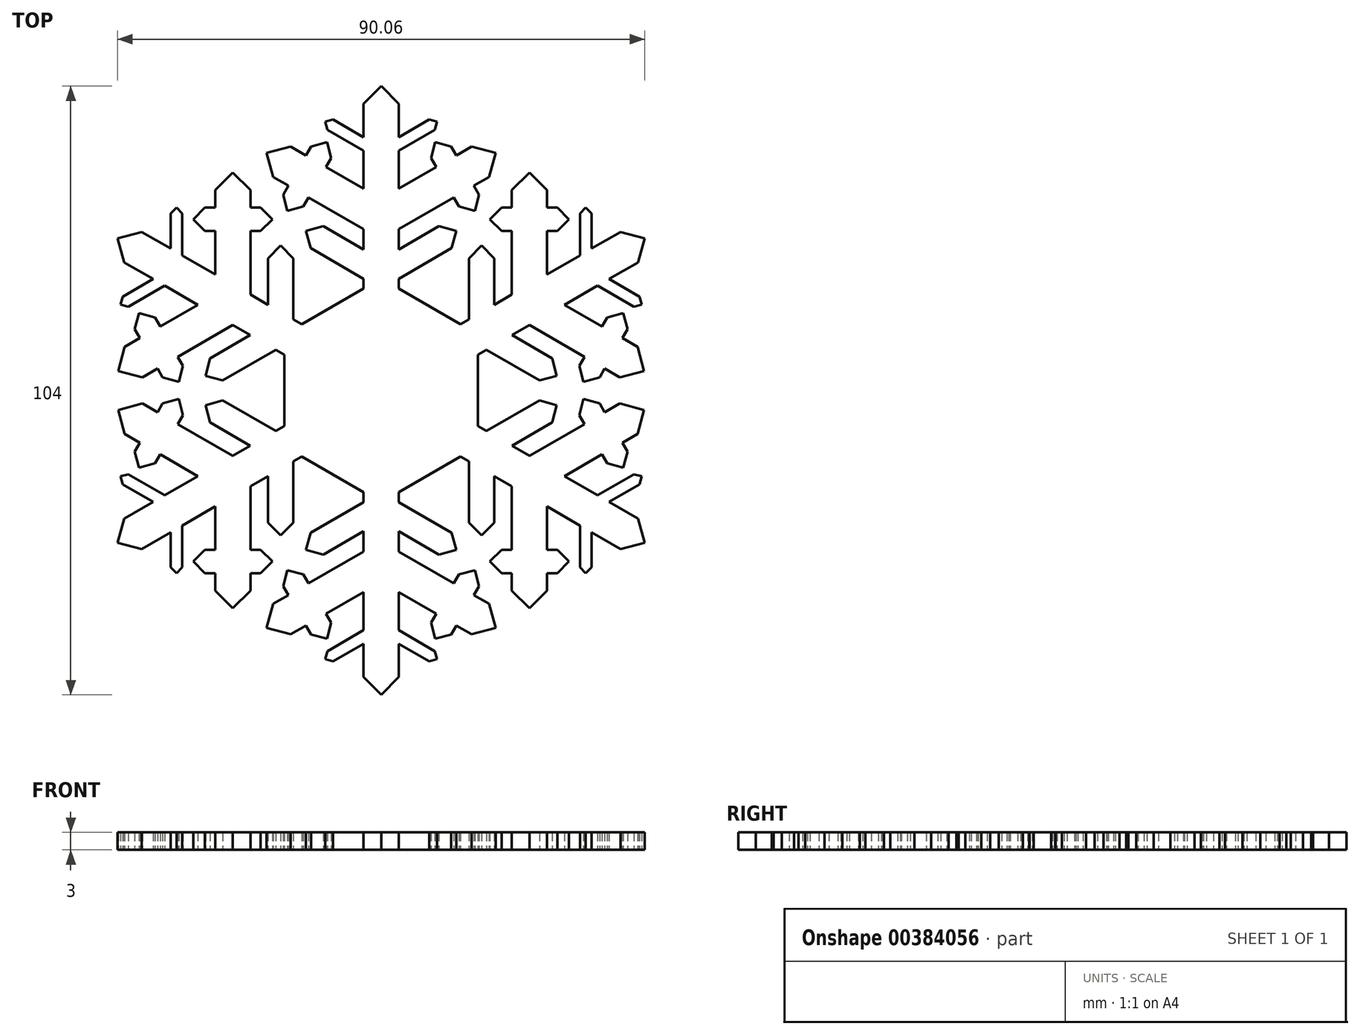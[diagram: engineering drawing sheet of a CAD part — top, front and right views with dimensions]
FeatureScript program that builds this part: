
annotation { "Feature Type Name" : "Feature", "Feature Type Description" : "" }
export const myFeature = defineFeature(function(context is Context, id is Id, definition is map)
    precondition{}
    {
        {
            var Q0;
            Q0=qCreatedBy(makeId("Top.planeOp"),FACE);
            var sketch = newSketch(context, id + "F0", { "sketchPlane" : qUnion([Q0])});
            skLineSegment(sketch, "E0", {"start": v(0, 26) * mm, "end": v(0, -26) * mm, "construction": true});
            skLineSegment(sketch, "E1", {"start": v(-22.52, -13) * mm, "end": v(22.52, 13) * mm, "construction": true});
            skLineSegment(sketch, "E2", {"start": v(22.52, -13) * mm, "end": v(-22.52, 13) * mm, "construction": true});
            skLineSegment(sketch, "E3", {"start": v(-1.5, 8.7) * mm, "end": v(-1.5, 9.54) * mm});
            skLineSegment(sketch, "E4", {"start": v(-1.5, 13.77) * mm, "end": v(-6.2, 16.48) * mm});
            skLineSegment(sketch, "E5", {"start": v(-6.2, 16.48) * mm, "end": v(-6.64, 15.72) * mm});
            skLineSegment(sketch, "E6", {"start": v(-6.64, 15.72) * mm, "end": v(-8, 15.35) * mm});
            skLineSegment(sketch, "E7", {"start": v(-8, 15.35) * mm, "end": v(-8.38, 16.72) * mm});
            skLineSegment(sketch, "E8", {"start": v(-8.38, 16.72) * mm, "end": v(-7.93, 17.48) * mm});
            skLineSegment(sketch, "E9", {"start": v(-7.93, 17.48) * mm, "end": v(-9.23, 18.23) * mm});
            skLineSegment(sketch, "E10", {"start": v(-9.23, 18.23) * mm, "end": v(-9.78, 20.28) * mm});
            skLineSegment(sketch, "E11", {"start": v(-9.78, 20.28) * mm, "end": v(0, 14.64) * mm, "construction": true});
            skLineSegment(sketch, "E12", {"start": v(-6.32, 18.28) * mm, "end": v(-8, 15.35) * mm, "construction": true});
            skLineSegment(sketch, "E13", {"start": v(-8.38, 16.72) * mm, "end": v(-6.64, 15.72) * mm, "construction": true});
            skPoint(sketch, "E14", {"position": v(-7.5, 16.22) * mm});
            skLineSegment(sketch, "E15.MirrorCS", {"start": v(-7.73, 20.83) * mm, "end": v(-9.78, 20.28) * mm});
            skLineSegment(sketch, "E16.MirrorCS", {"start": v(-6.43, 20.08) * mm, "end": v(-7.73, 20.83) * mm});
            skLineSegment(sketch, "E17.MirrorCS", {"start": v(-6, 20.85) * mm, "end": v(-6.43, 20.08) * mm});
            skLineSegment(sketch, "E18.MirrorCS", {"start": v(-4.63, 21.21) * mm, "end": v(-6, 20.85) * mm});
            skLineSegment(sketch, "E19.MirrorCS", {"start": v(-4.26, 19.85) * mm, "end": v(-4.63, 21.21) * mm});
            skLineSegment(sketch, "E20.MirrorCS", {"start": v(-4.7, 19.08) * mm, "end": v(-4.26, 19.85) * mm});
            skLineSegment(sketch, "E21.MirrorCS", {"start": v(-1.5, 17.23) * mm, "end": v(-4.7, 19.08) * mm});
            skLineSegment(sketch, "E22", {"start": v(-1.5, 17.23) * mm, "end": v(-1.5, 20.49) * mm});
            skLineSegment(sketch, "E23", {"start": v(-1.5, 20.49) * mm, "end": v(-4.6, 22.27) * mm});
            skLineSegment(sketch, "E24", {"start": v(-4.6, 22.27) * mm, "end": v(-4.78, 22.96) * mm});
            skLineSegment(sketch, "E25", {"start": v(-4.78, 22.96) * mm, "end": v(-4.1, 23.14) * mm});
            skLineSegment(sketch, "E26", {"start": v(-4.1, 23.14) * mm, "end": v(-1.5, 21.64) * mm});
            skLineSegment(sketch, "E27", {"start": v(-1.5, 21.64) * mm, "end": v(-1.5, 24.48) * mm});
            skLineSegment(sketch, "E28", {"start": v(-1.5, 24.48) * mm, "end": v(0, 26) * mm});
            skLineSegment(sketch, "E29", {"start": v(-4.6, 22.27) * mm, "end": v(-4.1, 23.14) * mm, "construction": true});
            skLineSegment(sketch, "E30", {"start": v(-4.78, 22.96) * mm, "end": v(-4.35, 22.7) * mm, "construction": true});
            skPoint(sketch, "E31.orphan", {"position": v(0, 16.37) * mm});
            skLineSegment(sketch, "E32", {"start": v(0, 9.56) * mm, "end": v(-8.28, 4.78) * mm});
            skLineSegment(sketch, "E33", {"start": v(-1.5, 12.04) * mm, "end": v(-4.94, 14.03) * mm});
            skLineSegment(sketch, "E34", {"start": v(-4.94, 14.03) * mm, "end": v(-6.42, 13.63) * mm});
            skLineSegment(sketch, "E35", {"start": v(-6.42, 13.63) * mm, "end": v(-6.02, 12.15) * mm});
            skLineSegment(sketch, "E36", {"start": v(-6.02, 12.15) * mm, "end": v(-1.5, 9.54) * mm});
            skLineSegment(sketch, "E37", {"start": v(-6.02, 12.15) * mm, "end": v(-4.94, 14.03) * mm, "construction": true});
            skPoint(sketch, "E38.endSnap0", {"position": v(-5.48, 13.09) * mm});
            skLineSegment(sketch, "E39", {"start": v(-6.42, 13.63) * mm, "end": v(-5.48, 13.09) * mm, "construction": true});
            skLineSegment(sketch, "E40.trimOffspring", {"start": v(-1.5, 12.04) * mm, "end": v(-1.5, 13.77) * mm});
            skLineSegment(sketch, "E41.MirrorCS", {"start": v(4.6, 22.27) * mm, "end": v(4.1, 23.14) * mm, "construction": true});
            skLineSegment(sketch, "E42.MirrorCS", {"start": v(4.78, 22.96) * mm, "end": v(4.1, 23.14) * mm});
            skLineSegment(sketch, "E43.MirrorCS", {"start": v(4.6, 22.27) * mm, "end": v(4.78, 22.96) * mm});
            skLineSegment(sketch, "E44.MirrorCS", {"start": v(4.78, 22.96) * mm, "end": v(4.35, 22.7) * mm, "construction": true});
            skLineSegment(sketch, "E45.MirrorCS", {"start": v(6.02, 12.15) * mm, "end": v(4.94, 14.03) * mm, "construction": true});
            skLineSegment(sketch, "E46.MirrorCS", {"start": v(6.42, 13.63) * mm, "end": v(5.48, 13.09) * mm, "construction": true});
            skLineSegment(sketch, "E47.MirrorCS", {"start": v(8.38, 16.72) * mm, "end": v(6.64, 15.72) * mm, "construction": true});
            skLineSegment(sketch, "E48.MirrorCS", {"start": v(4.94, 14.03) * mm, "end": v(6.42, 13.63) * mm});
            skLineSegment(sketch, "E49.MirrorCS", {"start": v(1.5, 21.64) * mm, "end": v(1.5, 24.48) * mm});
            skLineSegment(sketch, "E50.MirrorCS", {"start": v(6, 20.85) * mm, "end": v(6.43, 20.08) * mm});
            skLineSegment(sketch, "E51.MirrorCS", {"start": v(6.02, 12.15) * mm, "end": v(1.5, 9.54) * mm});
            skLineSegment(sketch, "E52.MirrorCS", {"start": v(4.63, 21.21) * mm, "end": v(6, 20.85) * mm});
            skLineSegment(sketch, "E53.MirrorCS", {"start": v(7.73, 20.83) * mm, "end": v(9.78, 20.28) * mm});
            skLineSegment(sketch, "E54.MirrorCS", {"start": v(0, 9.56) * mm, "end": v(8.28, 4.78) * mm});
            skLineSegment(sketch, "E55.MirrorCS", {"start": v(1.5, 20.49) * mm, "end": v(4.6, 22.27) * mm});
            skLineSegment(sketch, "E56.MirrorCS", {"start": v(1.5, 12.04) * mm, "end": v(4.94, 14.03) * mm});
            skLineSegment(sketch, "E57.MirrorCS", {"start": v(1.5, 24.48) * mm, "end": v(0, 26) * mm});
            skLineSegment(sketch, "E58.MirrorCS", {"start": v(1.5, 12.04) * mm, "end": v(1.5, 13.77) * mm});
            skPoint(sketch, "E59.MirrorP", {"position": v(7.5, 16.22) * mm});
            skLineSegment(sketch, "E60.MirrorCS", {"start": v(1.5, 17.23) * mm, "end": v(4.7, 19.08) * mm});
            skLineSegment(sketch, "E61.MirrorCS", {"start": v(4.1, 23.14) * mm, "end": v(1.5, 21.64) * mm});
            skLineSegment(sketch, "E62.MirrorCS", {"start": v(6.32, 18.28) * mm, "end": v(8, 15.35) * mm, "construction": true});
            skLineSegment(sketch, "E63.MirrorCS", {"start": v(9.78, 20.28) * mm, "end": v(0, 14.64) * mm, "construction": true});
            skLineSegment(sketch, "E64.MirrorCS", {"start": v(9.23, 18.23) * mm, "end": v(9.78, 20.28) * mm});
            skLineSegment(sketch, "E65.MirrorCS", {"start": v(6.43, 20.08) * mm, "end": v(7.73, 20.83) * mm});
            skLineSegment(sketch, "E66.MirrorCS", {"start": v(8.38, 16.72) * mm, "end": v(7.93, 17.48) * mm});
            skPoint(sketch, "E67.MirrorP", {"position": v(5.48, 13.09) * mm});
            skLineSegment(sketch, "E68.MirrorCS", {"start": v(1.5, 17.23) * mm, "end": v(1.5, 20.49) * mm});
            skLineSegment(sketch, "E69.MirrorCS", {"start": v(7.93, 17.48) * mm, "end": v(9.23, 18.23) * mm});
            skLineSegment(sketch, "E70.MirrorCS", {"start": v(8, 15.35) * mm, "end": v(8.38, 16.72) * mm});
            skLineSegment(sketch, "E71.MirrorCS", {"start": v(6.42, 13.63) * mm, "end": v(6.02, 12.15) * mm});
            skLineSegment(sketch, "E72.MirrorCS", {"start": v(4.26, 19.85) * mm, "end": v(4.63, 21.21) * mm});
            skLineSegment(sketch, "E73.MirrorCS", {"start": v(4.7, 19.08) * mm, "end": v(4.26, 19.85) * mm});
            skLineSegment(sketch, "E74.MirrorCS", {"start": v(1.5, 8.7) * mm, "end": v(1.5, 9.54) * mm});
            skLineSegment(sketch, "E75.MirrorCS", {"start": v(6.64, 15.72) * mm, "end": v(8, 15.35) * mm});
            skLineSegment(sketch, "E76.MirrorCS", {"start": v(1.5, 13.77) * mm, "end": v(6.2, 16.48) * mm});
            skLineSegment(sketch, "E77.MirrorCS", {"start": v(6.2, 16.48) * mm, "end": v(6.64, 15.72) * mm});
            skLineSegment(sketch, "E78.1.0", {"start": v(-14.18, 13.61) * mm, "end": v(-15.06, 13.61) * mm});
            skLineSegment(sketch, "E78.1.1", {"start": v(-21.95, 10.94) * mm, "end": v(-22.52, 13) * mm});
            skLineSegment(sketch, "E78.1.2", {"start": v(-14.18, 15.61) * mm, "end": v(-14.18, 17.11) * mm});
            skLineSegment(sketch, "E78.1.3", {"start": v(-17, 11.54) * mm, "end": v(-17, 15.12) * mm});
            skLineSegment(sketch, "E78.1.4", {"start": v(-12.68, 14.61) * mm, "end": v(-9.3, 14.61) * mm, "construction": true});
            skLineSegment(sketch, "E78.1.5", {"start": v(-15.68, 7.32) * mm, "end": v(-18.88, 5.47) * mm});
            skPoint(sketch, "E78.1.6", {"position": v(-8.6, 11.29) * mm});
            skLineSegment(sketch, "E78.1.7", {"start": v(-11.18, 17.11) * mm, "end": v(-12.68, 18.61) * mm});
            skLineSegment(sketch, "E78.1.8", {"start": v(-12.68, 18.61) * mm, "end": v(-12.68, 7.32) * mm, "construction": true});
            skLineSegment(sketch, "E78.1.9", {"start": v(-9.68, 11.29) * mm, "end": v(-8.6, 12.37) * mm});
            skLineSegment(sketch, "E78.1.10", {"start": v(-18.88, 5.47) * mm, "end": v(-19.32, 6.23) * mm});
            skLineSegment(sketch, "E78.1.11", {"start": v(-8.28, 4.78) * mm, "end": v(-8.28, -4.78) * mm});
            skPoint(sketch, "E78.1.12", {"position": v(-14.07, 1.8) * mm});
            skLineSegment(sketch, "E78.1.13", {"start": v(-11.18, 4.72) * mm, "end": v(-12.68, 5.59) * mm});
            skLineSegment(sketch, "E78.1.14", {"start": v(-6.78, 5.64) * mm, "end": v(-7.51, 6.07) * mm});
            skLineSegment(sketch, "E78.1.15", {"start": v(-19.5, 9.52) * mm, "end": v(-21.95, 10.94) * mm});
            skLineSegment(sketch, "E78.1.16", {"start": v(-15.06, 15.61) * mm, "end": v(-14.18, 15.61) * mm});
            skLineSegment(sketch, "E78.1.17", {"start": v(-20.45, 13.54) * mm, "end": v(-22.52, 13) * mm});
            skLineSegment(sketch, "E78.1.18", {"start": v(-10.3, 13.61) * mm, "end": v(-9.3, 14.61) * mm});
            skPoint(sketch, "E78.1.19", {"position": v(-10.3, 14.61) * mm});
            skLineSegment(sketch, "E78.1.20", {"start": v(-18, 12.12) * mm, "end": v(-20.45, 13.54) * mm});
            skLineSegment(sketch, "E78.1.21", {"start": v(-15.06, 13.61) * mm, "end": v(-16.06, 14.61) * mm});
            skLineSegment(sketch, "E78.1.22", {"start": v(-10.3, 15.61) * mm, "end": v(-11.18, 15.61) * mm});
            skLineSegment(sketch, "E78.1.23", {"start": v(-18.5, 8.94) * mm, "end": v(-21.59, 7.16) * mm});
            skLineSegment(sketch, "E78.1.24", {"start": v(-15.68, 7.32) * mm, "end": v(-18.5, 8.94) * mm});
            skLineSegment(sketch, "E78.1.25", {"start": v(-8.28, 4.78) * mm, "end": v(0, 9.56) * mm});
            skLineSegment(sketch, "E78.1.26", {"start": v(-9.68, 7.32) * mm, "end": v(-9.68, 11.29) * mm});
            skLineSegment(sketch, "E78.1.27", {"start": v(-14.18, 9.92) * mm, "end": v(-17, 11.54) * mm});
            skLineSegment(sketch, "E78.1.28", {"start": v(-11.18, 4.72) * mm, "end": v(-14.62, 2.74) * mm});
            skLineSegment(sketch, "E78.1.29", {"start": v(-21.9, 3.72) * mm, "end": v(-22.46, 1.67) * mm});
            skLineSegment(sketch, "E78.1.30", {"start": v(-20.6, 4.47) * mm, "end": v(-21.9, 3.72) * mm});
            skLineSegment(sketch, "E78.1.31", {"start": v(-8.28, 3.05) * mm, "end": v(-9.01, 3.47) * mm});
            skLineSegment(sketch, "E78.1.32", {"start": v(-12.68, 5.59) * mm, "end": v(-17.38, 2.87) * mm});
            skLineSegment(sketch, "E78.1.33", {"start": v(-17.38, 2.87) * mm, "end": v(-16.94, 2.1) * mm});
            skLineSegment(sketch, "E78.1.34", {"start": v(-16.94, 2.1) * mm, "end": v(-17.3, 0.74) * mm});
            skLineSegment(sketch, "E78.1.35", {"start": v(-17.3, 0.74) * mm, "end": v(-18.67, 1.1) * mm});
            skLineSegment(sketch, "E78.1.36", {"start": v(-18.67, 1.1) * mm, "end": v(-19.1, 1.87) * mm});
            skLineSegment(sketch, "E78.1.37", {"start": v(-19.1, 1.87) * mm, "end": v(-20.4, 1.12) * mm});
            skLineSegment(sketch, "E78.1.38", {"start": v(-20.4, 1.12) * mm, "end": v(-22.46, 1.67) * mm});
            skLineSegment(sketch, "E78.1.39", {"start": v(-22.46, 1.67) * mm, "end": v(-12.68, 7.32) * mm, "construction": true});
            skLineSegment(sketch, "E78.1.40", {"start": v(-19, 3.67) * mm, "end": v(-17.3, 0.74) * mm, "construction": true});
            skPoint(sketch, "E78.1.41", {"position": v(-14.18, 8.18) * mm});
            skLineSegment(sketch, "E78.1.42", {"start": v(-9.68, 7.32) * mm, "end": v(-11.18, 8.18) * mm});
            skLineSegment(sketch, "E78.1.43", {"start": v(-11.18, 8.18) * mm, "end": v(-11.18, 13.61) * mm});
            skLineSegment(sketch, "E78.1.44", {"start": v(-21.05, 5.23) * mm, "end": v(-20.6, 4.47) * mm});
            skLineSegment(sketch, "E78.1.45", {"start": v(-11.18, 15.61) * mm, "end": v(-11.18, 17.11) * mm});
            skLineSegment(sketch, "E78.1.46", {"start": v(-7.51, 11.29) * mm, "end": v(-7.51, 6.07) * mm});
            skLineSegment(sketch, "E78.1.47", {"start": v(-14.62, 2.74) * mm, "end": v(-15.01, 1.26) * mm});
            skLineSegment(sketch, "E78.1.48", {"start": v(-14.18, 9.92) * mm, "end": v(-14.18, 13.61) * mm});
            skLineSegment(sketch, "E78.1.49", {"start": v(-11.18, 13.61) * mm, "end": v(-10.3, 13.61) * mm});
            skLineSegment(sketch, "E78.1.50", {"start": v(-20.68, 6.6) * mm, "end": v(-21.05, 5.23) * mm});
            skLineSegment(sketch, "E78.1.51", {"start": v(-9.3, 14.61) * mm, "end": v(-10.3, 15.61) * mm});
            skLineSegment(sketch, "E78.1.52", {"start": v(-16.06, 14.61) * mm, "end": v(-15.06, 15.61) * mm});
            skLineSegment(sketch, "E78.1.53", {"start": v(-15.01, 1.26) * mm, "end": v(-13.53, 0.86) * mm});
            skPoint(sketch, "E78.1.54", {"position": v(-17.8, 1.6) * mm});
            skLineSegment(sketch, "E78.1.55", {"start": v(-18, 15.12) * mm, "end": v(-18, 12.12) * mm});
            skLineSegment(sketch, "E78.1.56", {"start": v(-22.09, 8.02) * mm, "end": v(-19.5, 9.52) * mm});
            skLineSegment(sketch, "E78.1.57", {"start": v(-19.32, 6.23) * mm, "end": v(-20.68, 6.6) * mm});
            skLineSegment(sketch, "E78.1.58", {"start": v(-8.6, 12.37) * mm, "end": v(-7.51, 11.29) * mm});
            skLineSegment(sketch, "E78.1.59", {"start": v(-14.18, 17.11) * mm, "end": v(-12.68, 18.61) * mm});
            skLineSegment(sketch, "E78.1.60", {"start": v(-13.53, 0.86) * mm, "end": v(-9.01, 3.47) * mm});
            skPoint(sketch, "E78.1.61", {"position": v(-14.18, 8.18) * mm});
            skLineSegment(sketch, "E78.1.62", {"start": v(-10.3, 15.61) * mm, "end": v(-10.3, 13.61) * mm, "construction": true});
            skLineSegment(sketch, "E78.1.63", {"start": v(-18.67, 1.1) * mm, "end": v(-16.94, 2.1) * mm, "construction": true});
            skLineSegment(sketch, "E78.1.64", {"start": v(-7.51, 11.29) * mm, "end": v(-9.68, 11.29) * mm, "construction": true});
            skLineSegment(sketch, "E78.1.65", {"start": v(-8.6, 12.37) * mm, "end": v(-8.6, 11.29) * mm, "construction": true});
            skLineSegment(sketch, "E78.1.66", {"start": v(-15.01, 1.26) * mm, "end": v(-14.07, 1.8) * mm, "construction": true});
            skLineSegment(sketch, "E78.1.67", {"start": v(-13.53, 0.86) * mm, "end": v(-14.62, 2.74) * mm, "construction": true});
            skLineSegment(sketch, "E78.1.68", {"start": v(-21.59, 7.16) * mm, "end": v(-22.09, 8.02) * mm, "construction": true});
            skLineSegment(sketch, "E78.1.69", {"start": v(-22.27, 7.34) * mm, "end": v(-21.84, 7.59) * mm, "construction": true});
            skLineSegment(sketch, "E78.1.70", {"start": v(-17, 15.12) * mm, "end": v(-18, 15.12) * mm, "construction": true});
            skLineSegment(sketch, "E78.1.71", {"start": v(-17.5, 15.62) * mm, "end": v(-18, 15.12) * mm});
            skLineSegment(sketch, "E78.1.72", {"start": v(-21.59, 7.16) * mm, "end": v(-22.27, 7.34) * mm});
            skLineSegment(sketch, "E78.1.73", {"start": v(-17, 15.12) * mm, "end": v(-17.5, 15.62) * mm});
            skLineSegment(sketch, "E78.1.74", {"start": v(-22.27, 7.34) * mm, "end": v(-22.09, 8.02) * mm});
            skLineSegment(sketch, "E78.1.75", {"start": v(-17.5, 15.62) * mm, "end": v(-17.5, 15.12) * mm, "construction": true});
            skLineSegment(sketch, "E78.2.0", {"start": v(-18.88, -5.47) * mm, "end": v(-19.32, -6.23) * mm});
            skLineSegment(sketch, "E78.2.1", {"start": v(-20.45, -13.54) * mm, "end": v(-22.52, -13) * mm});
            skLineSegment(sketch, "E78.2.2", {"start": v(-20.6, -4.47) * mm, "end": v(-21.9, -3.72) * mm});
            skLineSegment(sketch, "E78.2.3", {"start": v(-18.5, -8.94) * mm, "end": v(-21.59, -7.16) * mm});
            skLineSegment(sketch, "E78.2.4", {"start": v(-19, -3.67) * mm, "end": v(-17.3, -0.74) * mm, "construction": true});
            skLineSegment(sketch, "E78.2.5", {"start": v(-14.18, -9.92) * mm, "end": v(-14.18, -13.61) * mm});
            skPoint(sketch, "E78.2.6", {"position": v(-14.07, -1.8) * mm});
            skLineSegment(sketch, "E78.2.7", {"start": v(-20.4, -1.12) * mm, "end": v(-22.46, -1.67) * mm});
            skLineSegment(sketch, "E78.2.8", {"start": v(-22.46, -1.67) * mm, "end": v(-12.68, -7.32) * mm, "construction": true});
            skLineSegment(sketch, "E78.2.9", {"start": v(-14.62, -2.74) * mm, "end": v(-15.01, -1.26) * mm});
            skLineSegment(sketch, "E78.2.10", {"start": v(-14.18, -13.61) * mm, "end": v(-15.06, -13.61) * mm});
            skLineSegment(sketch, "E78.2.11", {"start": v(-8.28, -4.78) * mm, "end": v(0, -9.56) * mm});
            skPoint(sketch, "E78.2.12", {"position": v(-8.6, -11.29) * mm});
            skLineSegment(sketch, "E78.2.13", {"start": v(-9.68, -7.32) * mm, "end": v(-11.18, -8.18) * mm});
            skLineSegment(sketch, "E78.2.14", {"start": v(-8.28, -3.05) * mm, "end": v(-9.01, -3.47) * mm});
            skLineSegment(sketch, "E78.2.15", {"start": v(-18, -12.12) * mm, "end": v(-20.45, -13.54) * mm});
            skLineSegment(sketch, "E78.2.16", {"start": v(-21.05, -5.23) * mm, "end": v(-20.6, -4.47) * mm});
            skLineSegment(sketch, "E78.2.17", {"start": v(-21.95, -10.94) * mm, "end": v(-22.52, -13) * mm});
            skLineSegment(sketch, "E78.2.18", {"start": v(-16.94, -2.1) * mm, "end": v(-17.3, -0.74) * mm});
            skPoint(sketch, "E78.2.19", {"position": v(-17.8, -1.6) * mm});
            skLineSegment(sketch, "E78.2.20", {"start": v(-19.5, -9.52) * mm, "end": v(-21.95, -10.94) * mm});
            skLineSegment(sketch, "E78.2.21", {"start": v(-19.32, -6.23) * mm, "end": v(-20.68, -6.6) * mm});
            skLineSegment(sketch, "E78.2.22", {"start": v(-18.67, -1.1) * mm, "end": v(-19.1, -1.87) * mm});
            skLineSegment(sketch, "E78.2.23", {"start": v(-17, -11.54) * mm, "end": v(-17, -15.12) * mm});
            skLineSegment(sketch, "E78.2.24", {"start": v(-14.18, -9.92) * mm, "end": v(-17, -11.54) * mm});
            skLineSegment(sketch, "E78.2.25", {"start": v(-8.28, -4.78) * mm, "end": v(-8.28, 4.78) * mm});
            skLineSegment(sketch, "E78.2.26", {"start": v(-11.18, -4.72) * mm, "end": v(-14.62, -2.74) * mm});
            skLineSegment(sketch, "E78.2.27", {"start": v(-15.68, -7.32) * mm, "end": v(-18.5, -8.94) * mm});
            skLineSegment(sketch, "E78.2.28", {"start": v(-9.68, -7.32) * mm, "end": v(-9.68, -11.29) * mm});
            skLineSegment(sketch, "E78.2.29", {"start": v(-14.18, -17.11) * mm, "end": v(-12.68, -18.61) * mm});
            skLineSegment(sketch, "E78.2.30", {"start": v(-14.18, -15.61) * mm, "end": v(-14.18, -17.11) * mm});
            skLineSegment(sketch, "E78.2.31", {"start": v(-6.78, -5.64) * mm, "end": v(-7.51, -6.07) * mm});
            skLineSegment(sketch, "E78.2.32", {"start": v(-11.18, -8.18) * mm, "end": v(-11.18, -13.61) * mm});
            skLineSegment(sketch, "E78.2.33", {"start": v(-11.18, -13.61) * mm, "end": v(-10.3, -13.61) * mm});
            skLineSegment(sketch, "E78.2.34", {"start": v(-10.3, -13.61) * mm, "end": v(-9.3, -14.61) * mm});
            skLineSegment(sketch, "E78.2.35", {"start": v(-9.3, -14.61) * mm, "end": v(-10.3, -15.61) * mm});
            skLineSegment(sketch, "E78.2.36", {"start": v(-10.3, -15.61) * mm, "end": v(-11.18, -15.61) * mm});
            skLineSegment(sketch, "E78.2.37", {"start": v(-11.18, -15.61) * mm, "end": v(-11.18, -17.11) * mm});
            skLineSegment(sketch, "E78.2.38", {"start": v(-11.18, -17.11) * mm, "end": v(-12.68, -18.61) * mm});
            skLineSegment(sketch, "E78.2.39", {"start": v(-12.68, -18.61) * mm, "end": v(-12.68, -7.32) * mm, "construction": true});
            skLineSegment(sketch, "E78.2.40", {"start": v(-12.68, -14.61) * mm, "end": v(-9.3, -14.61) * mm, "construction": true});
            skPoint(sketch, "E78.2.41", {"position": v(-14.18, -8.18) * mm});
            skLineSegment(sketch, "E78.2.42", {"start": v(-11.18, -4.72) * mm, "end": v(-12.68, -5.59) * mm});
            skLineSegment(sketch, "E78.2.43", {"start": v(-12.68, -5.59) * mm, "end": v(-17.38, -2.87) * mm});
            skLineSegment(sketch, "E78.2.44", {"start": v(-15.06, -15.61) * mm, "end": v(-14.18, -15.61) * mm});
            skLineSegment(sketch, "E78.2.45", {"start": v(-19.1, -1.87) * mm, "end": v(-20.4, -1.12) * mm});
            skLineSegment(sketch, "E78.2.46", {"start": v(-13.53, -0.86) * mm, "end": v(-9.01, -3.47) * mm});
            skLineSegment(sketch, "E78.2.47", {"start": v(-9.68, -11.29) * mm, "end": v(-8.6, -12.37) * mm});
            skLineSegment(sketch, "E78.2.48", {"start": v(-15.68, -7.32) * mm, "end": v(-18.88, -5.47) * mm});
            skLineSegment(sketch, "E78.2.49", {"start": v(-17.38, -2.87) * mm, "end": v(-16.94, -2.1) * mm});
            skLineSegment(sketch, "E78.2.50", {"start": v(-16.06, -14.61) * mm, "end": v(-15.06, -15.61) * mm});
            skLineSegment(sketch, "E78.2.51", {"start": v(-17.3, -0.74) * mm, "end": v(-18.67, -1.1) * mm});
            skLineSegment(sketch, "E78.2.52", {"start": v(-20.68, -6.6) * mm, "end": v(-21.05, -5.23) * mm});
            skLineSegment(sketch, "E78.2.53", {"start": v(-8.6, -12.37) * mm, "end": v(-7.51, -11.29) * mm});
            skPoint(sketch, "E78.2.54", {"position": v(-10.3, -14.61) * mm});
            skLineSegment(sketch, "E78.2.55", {"start": v(-22.09, -8.02) * mm, "end": v(-19.5, -9.52) * mm});
            skLineSegment(sketch, "E78.2.56", {"start": v(-18, -15.12) * mm, "end": v(-18, -12.12) * mm});
            skLineSegment(sketch, "E78.2.57", {"start": v(-15.06, -13.61) * mm, "end": v(-16.06, -14.61) * mm});
            skLineSegment(sketch, "E78.2.58", {"start": v(-15.01, -1.26) * mm, "end": v(-13.53, -0.86) * mm});
            skLineSegment(sketch, "E78.2.59", {"start": v(-21.9, -3.72) * mm, "end": v(-22.46, -1.67) * mm});
            skLineSegment(sketch, "E78.2.60", {"start": v(-7.51, -11.29) * mm, "end": v(-7.51, -6.07) * mm});
            skPoint(sketch, "E78.2.61", {"position": v(-14.18, -8.18) * mm});
            skLineSegment(sketch, "E78.2.62", {"start": v(-18.67, -1.1) * mm, "end": v(-16.94, -2.1) * mm, "construction": true});
            skLineSegment(sketch, "E78.2.63", {"start": v(-10.3, -15.61) * mm, "end": v(-10.3, -13.61) * mm, "construction": true});
            skLineSegment(sketch, "E78.2.64", {"start": v(-13.53, -0.86) * mm, "end": v(-14.62, -2.74) * mm, "construction": true});
            skLineSegment(sketch, "E78.2.65", {"start": v(-15.01, -1.26) * mm, "end": v(-14.07, -1.8) * mm, "construction": true});
            skLineSegment(sketch, "E78.2.66", {"start": v(-8.6, -12.37) * mm, "end": v(-8.6, -11.29) * mm, "construction": true});
            skLineSegment(sketch, "E78.2.67", {"start": v(-7.51, -11.29) * mm, "end": v(-9.68, -11.29) * mm, "construction": true});
            skLineSegment(sketch, "E78.2.68", {"start": v(-17, -15.12) * mm, "end": v(-18, -15.12) * mm, "construction": true});
            skLineSegment(sketch, "E78.2.69", {"start": v(-17.5, -15.62) * mm, "end": v(-17.5, -15.12) * mm, "construction": true});
            skLineSegment(sketch, "E78.2.70", {"start": v(-21.59, -7.16) * mm, "end": v(-22.09, -8.02) * mm, "construction": true});
            skLineSegment(sketch, "E78.2.71", {"start": v(-22.27, -7.34) * mm, "end": v(-22.09, -8.02) * mm});
            skLineSegment(sketch, "E78.2.72", {"start": v(-17, -15.12) * mm, "end": v(-17.5, -15.62) * mm});
            skLineSegment(sketch, "E78.2.73", {"start": v(-21.59, -7.16) * mm, "end": v(-22.27, -7.34) * mm});
            skLineSegment(sketch, "E78.2.74", {"start": v(-17.5, -15.62) * mm, "end": v(-18, -15.12) * mm});
            skLineSegment(sketch, "E78.2.75", {"start": v(-22.27, -7.34) * mm, "end": v(-21.84, -7.59) * mm, "construction": true});
            skLineSegment(sketch, "E78.3.0", {"start": v(-4.7, -19.08) * mm, "end": v(-4.26, -19.85) * mm});
            skLineSegment(sketch, "E78.3.1", {"start": v(1.5, -24.48) * mm, "end": v(0, -26) * mm});
            skLineSegment(sketch, "E78.3.2", {"start": v(-6.43, -20.08) * mm, "end": v(-7.73, -20.83) * mm});
            skLineSegment(sketch, "E78.3.3", {"start": v(-1.5, -20.49) * mm, "end": v(-4.6, -22.27) * mm});
            skLineSegment(sketch, "E78.3.4", {"start": v(-6.32, -18.28) * mm, "end": v(-8, -15.35) * mm, "construction": true});
            skLineSegment(sketch, "E78.3.5", {"start": v(1.5, -17.23) * mm, "end": v(4.7, -19.08) * mm});
            skPoint(sketch, "E78.3.6", {"position": v(-5.48, -13.09) * mm});
            skLineSegment(sketch, "E78.3.7", {"start": v(-9.23, -18.23) * mm, "end": v(-9.78, -20.28) * mm});
            skLineSegment(sketch, "E78.3.8", {"start": v(-9.78, -20.28) * mm, "end": v(0, -14.64) * mm, "construction": true});
            skLineSegment(sketch, "E78.3.9", {"start": v(-4.94, -14.03) * mm, "end": v(-6.42, -13.63) * mm});
            skLineSegment(sketch, "E78.3.10", {"start": v(4.7, -19.08) * mm, "end": v(4.26, -19.85) * mm});
            skLineSegment(sketch, "E78.3.11", {"start": v(0, -9.56) * mm, "end": v(8.28, -4.78) * mm});
            skPoint(sketch, "E78.3.12", {"position": v(5.48, -13.09) * mm});
            skLineSegment(sketch, "E78.3.13", {"start": v(1.5, -12.04) * mm, "end": v(1.5, -13.77) * mm});
            skLineSegment(sketch, "E78.3.14", {"start": v(-1.5, -8.7) * mm, "end": v(-1.5, -9.54) * mm});
            skLineSegment(sketch, "E78.3.15", {"start": v(1.5, -21.64) * mm, "end": v(1.5, -24.48) * mm});
            skLineSegment(sketch, "E78.3.16", {"start": v(-6, -20.85) * mm, "end": v(-6.43, -20.08) * mm});
            skLineSegment(sketch, "E78.3.17", {"start": v(-1.5, -24.48) * mm, "end": v(0, -26) * mm});
            skLineSegment(sketch, "E78.3.18", {"start": v(-6.64, -15.72) * mm, "end": v(-8, -15.35) * mm});
            skPoint(sketch, "E78.3.19", {"position": v(-7.5, -16.22) * mm});
            skLineSegment(sketch, "E78.3.20", {"start": v(-1.5, -21.64) * mm, "end": v(-1.5, -24.48) * mm});
            skLineSegment(sketch, "E78.3.21", {"start": v(-4.26, -19.85) * mm, "end": v(-4.63, -21.21) * mm});
            skLineSegment(sketch, "E78.3.22", {"start": v(-8.38, -16.72) * mm, "end": v(-7.93, -17.48) * mm});
            skLineSegment(sketch, "E78.3.23", {"start": v(1.5, -20.49) * mm, "end": v(4.6, -22.27) * mm});
            skLineSegment(sketch, "E78.3.24", {"start": v(1.5, -17.23) * mm, "end": v(1.5, -20.49) * mm});
            skLineSegment(sketch, "E78.3.25", {"start": v(0, -9.56) * mm, "end": v(-8.28, -4.78) * mm});
            skLineSegment(sketch, "E78.3.26", {"start": v(-1.5, -12.04) * mm, "end": v(-4.94, -14.03) * mm});
            skLineSegment(sketch, "E78.3.27", {"start": v(-1.5, -17.23) * mm, "end": v(-1.5, -20.49) * mm});
            skLineSegment(sketch, "E78.3.28", {"start": v(1.5, -12.04) * mm, "end": v(4.94, -14.03) * mm});
            skLineSegment(sketch, "E78.3.29", {"start": v(7.73, -20.83) * mm, "end": v(9.78, -20.28) * mm});
            skLineSegment(sketch, "E78.3.30", {"start": v(6.43, -20.08) * mm, "end": v(7.73, -20.83) * mm});
            skLineSegment(sketch, "E78.3.31", {"start": v(1.5, -8.7) * mm, "end": v(1.5, -9.54) * mm});
            skLineSegment(sketch, "E78.3.32", {"start": v(1.5, -13.77) * mm, "end": v(6.2, -16.48) * mm});
            skLineSegment(sketch, "E78.3.33", {"start": v(6.2, -16.48) * mm, "end": v(6.64, -15.72) * mm});
            skLineSegment(sketch, "E78.3.34", {"start": v(6.64, -15.72) * mm, "end": v(8, -15.35) * mm});
            skLineSegment(sketch, "E78.3.35", {"start": v(8, -15.35) * mm, "end": v(8.38, -16.72) * mm});
            skLineSegment(sketch, "E78.3.36", {"start": v(8.38, -16.72) * mm, "end": v(7.93, -17.48) * mm});
            skLineSegment(sketch, "E78.3.37", {"start": v(7.93, -17.48) * mm, "end": v(9.23, -18.23) * mm});
            skLineSegment(sketch, "E78.3.38", {"start": v(9.23, -18.23) * mm, "end": v(9.78, -20.28) * mm});
            skLineSegment(sketch, "E78.3.39", {"start": v(9.78, -20.28) * mm, "end": v(0, -14.64) * mm, "construction": true});
            skLineSegment(sketch, "E78.3.40", {"start": v(6.32, -18.28) * mm, "end": v(8, -15.35) * mm, "construction": true});
            skPoint(sketch, "E78.3.41", {"position": v(0, -16.37) * mm});
            skLineSegment(sketch, "E78.3.42", {"start": v(-1.5, -12.04) * mm, "end": v(-1.5, -13.77) * mm});
            skLineSegment(sketch, "E78.3.43", {"start": v(-1.5, -13.77) * mm, "end": v(-6.2, -16.48) * mm});
            skLineSegment(sketch, "E78.3.44", {"start": v(6, -20.85) * mm, "end": v(6.43, -20.08) * mm});
            skLineSegment(sketch, "E78.3.45", {"start": v(-7.93, -17.48) * mm, "end": v(-9.23, -18.23) * mm});
            skLineSegment(sketch, "E78.3.46", {"start": v(-6.02, -12.15) * mm, "end": v(-1.5, -9.54) * mm});
            skLineSegment(sketch, "E78.3.47", {"start": v(4.94, -14.03) * mm, "end": v(6.42, -13.63) * mm});
            skLineSegment(sketch, "E78.3.48", {"start": v(-1.5, -17.23) * mm, "end": v(-4.7, -19.08) * mm});
            skLineSegment(sketch, "E78.3.49", {"start": v(-6.2, -16.48) * mm, "end": v(-6.64, -15.72) * mm});
            skLineSegment(sketch, "E78.3.50", {"start": v(4.63, -21.21) * mm, "end": v(6, -20.85) * mm});
            skLineSegment(sketch, "E78.3.51", {"start": v(-8, -15.35) * mm, "end": v(-8.38, -16.72) * mm});
            skLineSegment(sketch, "E78.3.52", {"start": v(-4.63, -21.21) * mm, "end": v(-6, -20.85) * mm});
            skLineSegment(sketch, "E78.3.53", {"start": v(6.42, -13.63) * mm, "end": v(6.02, -12.15) * mm});
            skPoint(sketch, "E78.3.54", {"position": v(7.5, -16.22) * mm});
            skLineSegment(sketch, "E78.3.55", {"start": v(-4.1, -23.14) * mm, "end": v(-1.5, -21.64) * mm});
            skLineSegment(sketch, "E78.3.56", {"start": v(4.1, -23.14) * mm, "end": v(1.5, -21.64) * mm});
            skLineSegment(sketch, "E78.3.57", {"start": v(4.26, -19.85) * mm, "end": v(4.63, -21.21) * mm});
            skLineSegment(sketch, "E78.3.58", {"start": v(-6.42, -13.63) * mm, "end": v(-6.02, -12.15) * mm});
            skLineSegment(sketch, "E78.3.59", {"start": v(-7.73, -20.83) * mm, "end": v(-9.78, -20.28) * mm});
            skLineSegment(sketch, "E78.3.60", {"start": v(6.02, -12.15) * mm, "end": v(1.5, -9.54) * mm});
            skPoint(sketch, "E78.3.61", {"position": v(0, -16.37) * mm});
            skLineSegment(sketch, "E78.3.62", {"start": v(-8.38, -16.72) * mm, "end": v(-6.64, -15.72) * mm, "construction": true});
            skLineSegment(sketch, "E78.3.63", {"start": v(8.38, -16.72) * mm, "end": v(6.64, -15.72) * mm, "construction": true});
            skLineSegment(sketch, "E78.3.64", {"start": v(-6.02, -12.15) * mm, "end": v(-4.94, -14.03) * mm, "construction": true});
            skLineSegment(sketch, "E78.3.65", {"start": v(-6.42, -13.63) * mm, "end": v(-5.48, -13.09) * mm, "construction": true});
            skLineSegment(sketch, "E78.3.66", {"start": v(6.42, -13.63) * mm, "end": v(5.48, -13.09) * mm, "construction": true});
            skLineSegment(sketch, "E78.3.67", {"start": v(6.02, -12.15) * mm, "end": v(4.94, -14.03) * mm, "construction": true});
            skLineSegment(sketch, "E78.3.68", {"start": v(4.6, -22.27) * mm, "end": v(4.1, -23.14) * mm, "construction": true});
            skLineSegment(sketch, "E78.3.69", {"start": v(4.78, -22.96) * mm, "end": v(4.35, -22.7) * mm, "construction": true});
            skLineSegment(sketch, "E78.3.70", {"start": v(-4.6, -22.27) * mm, "end": v(-4.1, -23.14) * mm, "construction": true});
            skLineSegment(sketch, "E78.3.71", {"start": v(-4.78, -22.96) * mm, "end": v(-4.1, -23.14) * mm});
            skLineSegment(sketch, "E78.3.72", {"start": v(4.6, -22.27) * mm, "end": v(4.78, -22.96) * mm});
            skLineSegment(sketch, "E78.3.73", {"start": v(-4.6, -22.27) * mm, "end": v(-4.78, -22.96) * mm});
            skLineSegment(sketch, "E78.3.74", {"start": v(4.78, -22.96) * mm, "end": v(4.1, -23.14) * mm});
            skLineSegment(sketch, "E78.3.75", {"start": v(-4.78, -22.96) * mm, "end": v(-4.35, -22.7) * mm, "construction": true});
            skLineSegment(sketch, "E78.4.0", {"start": v(14.18, -13.61) * mm, "end": v(15.06, -13.61) * mm});
            skLineSegment(sketch, "E78.4.1", {"start": v(21.95, -10.94) * mm, "end": v(22.52, -13) * mm});
            skLineSegment(sketch, "E78.4.2", {"start": v(14.18, -15.61) * mm, "end": v(14.18, -17.11) * mm});
            skLineSegment(sketch, "E78.4.3", {"start": v(17, -11.54) * mm, "end": v(17, -15.12) * mm});
            skLineSegment(sketch, "E78.4.4", {"start": v(12.68, -14.61) * mm, "end": v(9.3, -14.61) * mm, "construction": true});
            skLineSegment(sketch, "E78.4.5", {"start": v(15.68, -7.32) * mm, "end": v(18.88, -5.47) * mm});
            skPoint(sketch, "E78.4.6", {"position": v(8.6, -11.29) * mm});
            skLineSegment(sketch, "E78.4.7", {"start": v(11.18, -17.11) * mm, "end": v(12.68, -18.61) * mm});
            skLineSegment(sketch, "E78.4.8", {"start": v(12.68, -18.61) * mm, "end": v(12.68, -7.32) * mm, "construction": true});
            skLineSegment(sketch, "E78.4.9", {"start": v(9.68, -11.29) * mm, "end": v(8.6, -12.37) * mm});
            skLineSegment(sketch, "E78.4.10", {"start": v(18.88, -5.47) * mm, "end": v(19.32, -6.23) * mm});
            skLineSegment(sketch, "E78.4.11", {"start": v(8.28, -4.78) * mm, "end": v(8.28, 4.78) * mm});
            skPoint(sketch, "E78.4.12", {"position": v(14.07, -1.8) * mm});
            skLineSegment(sketch, "E78.4.13", {"start": v(11.18, -4.72) * mm, "end": v(12.68, -5.59) * mm});
            skLineSegment(sketch, "E78.4.14", {"start": v(6.78, -5.64) * mm, "end": v(7.51, -6.07) * mm});
            skLineSegment(sketch, "E78.4.15", {"start": v(19.5, -9.52) * mm, "end": v(21.95, -10.94) * mm});
            skLineSegment(sketch, "E78.4.16", {"start": v(15.06, -15.61) * mm, "end": v(14.18, -15.61) * mm});
            skLineSegment(sketch, "E78.4.17", {"start": v(20.45, -13.54) * mm, "end": v(22.52, -13) * mm});
            skLineSegment(sketch, "E78.4.18", {"start": v(10.3, -13.61) * mm, "end": v(9.3, -14.61) * mm});
            skPoint(sketch, "E78.4.19", {"position": v(10.3, -14.61) * mm});
            skLineSegment(sketch, "E78.4.20", {"start": v(18, -12.12) * mm, "end": v(20.45, -13.54) * mm});
            skLineSegment(sketch, "E78.4.21", {"start": v(15.06, -13.61) * mm, "end": v(16.06, -14.61) * mm});
            skLineSegment(sketch, "E78.4.22", {"start": v(10.3, -15.61) * mm, "end": v(11.18, -15.61) * mm});
            skLineSegment(sketch, "E78.4.23", {"start": v(18.5, -8.94) * mm, "end": v(21.59, -7.16) * mm});
            skLineSegment(sketch, "E78.4.24", {"start": v(15.68, -7.32) * mm, "end": v(18.5, -8.94) * mm});
            skLineSegment(sketch, "E78.4.25", {"start": v(8.28, -4.78) * mm, "end": v(0, -9.56) * mm});
            skLineSegment(sketch, "E78.4.26", {"start": v(9.68, -7.32) * mm, "end": v(9.68, -11.29) * mm});
            skLineSegment(sketch, "E78.4.27", {"start": v(14.18, -9.92) * mm, "end": v(17, -11.54) * mm});
            skLineSegment(sketch, "E78.4.28", {"start": v(11.18, -4.72) * mm, "end": v(14.62, -2.74) * mm});
            skLineSegment(sketch, "E78.4.29", {"start": v(21.9, -3.72) * mm, "end": v(22.46, -1.67) * mm});
            skLineSegment(sketch, "E78.4.30", {"start": v(20.6, -4.47) * mm, "end": v(21.9, -3.72) * mm});
            skLineSegment(sketch, "E78.4.31", {"start": v(8.28, -3.05) * mm, "end": v(9.01, -3.47) * mm});
            skLineSegment(sketch, "E78.4.32", {"start": v(12.68, -5.59) * mm, "end": v(17.38, -2.87) * mm});
            skLineSegment(sketch, "E78.4.33", {"start": v(17.38, -2.87) * mm, "end": v(16.94, -2.1) * mm});
            skLineSegment(sketch, "E78.4.34", {"start": v(16.94, -2.1) * mm, "end": v(17.3, -0.74) * mm});
            skLineSegment(sketch, "E78.4.35", {"start": v(17.3, -0.74) * mm, "end": v(18.67, -1.1) * mm});
            skLineSegment(sketch, "E78.4.36", {"start": v(18.67, -1.1) * mm, "end": v(19.1, -1.87) * mm});
            skLineSegment(sketch, "E78.4.37", {"start": v(19.1, -1.87) * mm, "end": v(20.4, -1.12) * mm});
            skLineSegment(sketch, "E78.4.38", {"start": v(20.4, -1.12) * mm, "end": v(22.46, -1.67) * mm});
            skLineSegment(sketch, "E78.4.39", {"start": v(22.46, -1.67) * mm, "end": v(12.68, -7.32) * mm, "construction": true});
            skLineSegment(sketch, "E78.4.40", {"start": v(19, -3.67) * mm, "end": v(17.3, -0.74) * mm, "construction": true});
            skPoint(sketch, "E78.4.41", {"position": v(14.18, -8.18) * mm});
            skLineSegment(sketch, "E78.4.42", {"start": v(9.68, -7.32) * mm, "end": v(11.18, -8.18) * mm});
            skLineSegment(sketch, "E78.4.43", {"start": v(11.18, -8.18) * mm, "end": v(11.18, -13.61) * mm});
            skLineSegment(sketch, "E78.4.44", {"start": v(21.05, -5.23) * mm, "end": v(20.6, -4.47) * mm});
            skLineSegment(sketch, "E78.4.45", {"start": v(11.18, -15.61) * mm, "end": v(11.18, -17.11) * mm});
            skLineSegment(sketch, "E78.4.46", {"start": v(7.51, -11.29) * mm, "end": v(7.51, -6.07) * mm});
            skLineSegment(sketch, "E78.4.47", {"start": v(14.62, -2.74) * mm, "end": v(15.01, -1.26) * mm});
            skLineSegment(sketch, "E78.4.48", {"start": v(14.18, -9.92) * mm, "end": v(14.18, -13.61) * mm});
            skLineSegment(sketch, "E78.4.49", {"start": v(11.18, -13.61) * mm, "end": v(10.3, -13.61) * mm});
            skLineSegment(sketch, "E78.4.50", {"start": v(20.68, -6.6) * mm, "end": v(21.05, -5.23) * mm});
            skLineSegment(sketch, "E78.4.51", {"start": v(9.3, -14.61) * mm, "end": v(10.3, -15.61) * mm});
            skLineSegment(sketch, "E78.4.52", {"start": v(16.06, -14.61) * mm, "end": v(15.06, -15.61) * mm});
            skLineSegment(sketch, "E78.4.53", {"start": v(15.01, -1.26) * mm, "end": v(13.53, -0.86) * mm});
            skPoint(sketch, "E78.4.54", {"position": v(17.8, -1.6) * mm});
            skLineSegment(sketch, "E78.4.55", {"start": v(18, -15.12) * mm, "end": v(18, -12.12) * mm});
            skLineSegment(sketch, "E78.4.56", {"start": v(22.09, -8.02) * mm, "end": v(19.5, -9.52) * mm});
            skLineSegment(sketch, "E78.4.57", {"start": v(19.32, -6.23) * mm, "end": v(20.68, -6.6) * mm});
            skLineSegment(sketch, "E78.4.58", {"start": v(8.6, -12.37) * mm, "end": v(7.51, -11.29) * mm});
            skLineSegment(sketch, "E78.4.59", {"start": v(14.18, -17.11) * mm, "end": v(12.68, -18.61) * mm});
            skLineSegment(sketch, "E78.4.60", {"start": v(13.53, -0.86) * mm, "end": v(9.01, -3.47) * mm});
            skPoint(sketch, "E78.4.61", {"position": v(14.18, -8.18) * mm});
            skLineSegment(sketch, "E78.4.62", {"start": v(10.3, -15.61) * mm, "end": v(10.3, -13.61) * mm, "construction": true});
            skLineSegment(sketch, "E78.4.63", {"start": v(18.67, -1.1) * mm, "end": v(16.94, -2.1) * mm, "construction": true});
            skLineSegment(sketch, "E78.4.64", {"start": v(7.51, -11.29) * mm, "end": v(9.68, -11.29) * mm, "construction": true});
            skLineSegment(sketch, "E78.4.65", {"start": v(8.6, -12.37) * mm, "end": v(8.6, -11.29) * mm, "construction": true});
            skLineSegment(sketch, "E78.4.66", {"start": v(15.01, -1.26) * mm, "end": v(14.07, -1.8) * mm, "construction": true});
            skLineSegment(sketch, "E78.4.67", {"start": v(13.53, -0.86) * mm, "end": v(14.62, -2.74) * mm, "construction": true});
            skLineSegment(sketch, "E78.4.68", {"start": v(21.59, -7.16) * mm, "end": v(22.09, -8.02) * mm, "construction": true});
            skLineSegment(sketch, "E78.4.69", {"start": v(22.27, -7.34) * mm, "end": v(21.84, -7.59) * mm, "construction": true});
            skLineSegment(sketch, "E78.4.70", {"start": v(17, -15.12) * mm, "end": v(18, -15.12) * mm, "construction": true});
            skLineSegment(sketch, "E78.4.71", {"start": v(17.5, -15.62) * mm, "end": v(18, -15.12) * mm});
            skLineSegment(sketch, "E78.4.72", {"start": v(21.59, -7.16) * mm, "end": v(22.27, -7.34) * mm});
            skLineSegment(sketch, "E78.4.73", {"start": v(17, -15.12) * mm, "end": v(17.5, -15.62) * mm});
            skLineSegment(sketch, "E78.4.74", {"start": v(22.27, -7.34) * mm, "end": v(22.09, -8.02) * mm});
            skLineSegment(sketch, "E78.4.75", {"start": v(17.5, -15.62) * mm, "end": v(17.5, -15.12) * mm, "construction": true});
            skLineSegment(sketch, "E78.5.0", {"start": v(18.88, 5.47) * mm, "end": v(19.32, 6.23) * mm});
            skLineSegment(sketch, "E78.5.1", {"start": v(20.45, 13.54) * mm, "end": v(22.52, 13) * mm});
            skLineSegment(sketch, "E78.5.2", {"start": v(20.6, 4.47) * mm, "end": v(21.9, 3.72) * mm});
            skLineSegment(sketch, "E78.5.3", {"start": v(18.5, 8.94) * mm, "end": v(21.59, 7.16) * mm});
            skLineSegment(sketch, "E78.5.4", {"start": v(19, 3.67) * mm, "end": v(17.3, 0.74) * mm, "construction": true});
            skLineSegment(sketch, "E78.5.5", {"start": v(14.18, 9.92) * mm, "end": v(14.18, 13.61) * mm});
            skPoint(sketch, "E78.5.6", {"position": v(14.07, 1.8) * mm});
            skLineSegment(sketch, "E78.5.7", {"start": v(20.4, 1.12) * mm, "end": v(22.46, 1.67) * mm});
            skLineSegment(sketch, "E78.5.8", {"start": v(22.46, 1.67) * mm, "end": v(12.68, 7.32) * mm, "construction": true});
            skLineSegment(sketch, "E78.5.9", {"start": v(14.62, 2.74) * mm, "end": v(15.01, 1.26) * mm});
            skLineSegment(sketch, "E78.5.10", {"start": v(14.18, 13.61) * mm, "end": v(15.06, 13.61) * mm});
            skLineSegment(sketch, "E78.5.11", {"start": v(8.28, 4.78) * mm, "end": v(0, 9.56) * mm});
            skPoint(sketch, "E78.5.12", {"position": v(8.6, 11.29) * mm});
            skLineSegment(sketch, "E78.5.13", {"start": v(9.68, 7.32) * mm, "end": v(11.18, 8.18) * mm});
            skLineSegment(sketch, "E78.5.14", {"start": v(8.28, 3.05) * mm, "end": v(9.01, 3.47) * mm});
            skLineSegment(sketch, "E78.5.15", {"start": v(18, 12.12) * mm, "end": v(20.45, 13.54) * mm});
            skLineSegment(sketch, "E78.5.16", {"start": v(21.05, 5.23) * mm, "end": v(20.6, 4.47) * mm});
            skLineSegment(sketch, "E78.5.17", {"start": v(21.95, 10.94) * mm, "end": v(22.52, 13) * mm});
            skLineSegment(sketch, "E78.5.18", {"start": v(16.94, 2.1) * mm, "end": v(17.3, 0.74) * mm});
            skPoint(sketch, "E78.5.19", {"position": v(17.8, 1.6) * mm});
            skLineSegment(sketch, "E78.5.20", {"start": v(19.5, 9.52) * mm, "end": v(21.95, 10.94) * mm});
            skLineSegment(sketch, "E78.5.21", {"start": v(19.32, 6.23) * mm, "end": v(20.68, 6.6) * mm});
            skLineSegment(sketch, "E78.5.22", {"start": v(18.67, 1.1) * mm, "end": v(19.1, 1.87) * mm});
            skLineSegment(sketch, "E78.5.23", {"start": v(17, 11.54) * mm, "end": v(17, 15.12) * mm});
            skLineSegment(sketch, "E78.5.24", {"start": v(14.18, 9.92) * mm, "end": v(17, 11.54) * mm});
            skLineSegment(sketch, "E78.5.25", {"start": v(8.28, 4.78) * mm, "end": v(8.28, -4.78) * mm});
            skLineSegment(sketch, "E78.5.26", {"start": v(11.18, 4.72) * mm, "end": v(14.62, 2.74) * mm});
            skLineSegment(sketch, "E78.5.27", {"start": v(15.68, 7.32) * mm, "end": v(18.5, 8.94) * mm});
            skLineSegment(sketch, "E78.5.28", {"start": v(9.68, 7.32) * mm, "end": v(9.68, 11.29) * mm});
            skLineSegment(sketch, "E78.5.29", {"start": v(14.18, 17.11) * mm, "end": v(12.68, 18.61) * mm});
            skLineSegment(sketch, "E78.5.30", {"start": v(14.18, 15.61) * mm, "end": v(14.18, 17.11) * mm});
            skLineSegment(sketch, "E78.5.31", {"start": v(6.78, 5.64) * mm, "end": v(7.51, 6.07) * mm});
            skLineSegment(sketch, "E78.5.32", {"start": v(11.18, 8.18) * mm, "end": v(11.18, 13.61) * mm});
            skLineSegment(sketch, "E78.5.33", {"start": v(11.18, 13.61) * mm, "end": v(10.3, 13.61) * mm});
            skLineSegment(sketch, "E78.5.34", {"start": v(10.3, 13.61) * mm, "end": v(9.3, 14.61) * mm});
            skLineSegment(sketch, "E78.5.35", {"start": v(9.3, 14.61) * mm, "end": v(10.3, 15.61) * mm});
            skLineSegment(sketch, "E78.5.36", {"start": v(10.3, 15.61) * mm, "end": v(11.18, 15.61) * mm});
            skLineSegment(sketch, "E78.5.37", {"start": v(11.18, 15.61) * mm, "end": v(11.18, 17.11) * mm});
            skLineSegment(sketch, "E78.5.38", {"start": v(11.18, 17.11) * mm, "end": v(12.68, 18.61) * mm});
            skLineSegment(sketch, "E78.5.39", {"start": v(12.68, 18.61) * mm, "end": v(12.68, 7.32) * mm, "construction": true});
            skLineSegment(sketch, "E78.5.40", {"start": v(12.68, 14.61) * mm, "end": v(9.3, 14.61) * mm, "construction": true});
            skPoint(sketch, "E78.5.41", {"position": v(14.18, 8.18) * mm});
            skLineSegment(sketch, "E78.5.42", {"start": v(11.18, 4.72) * mm, "end": v(12.68, 5.59) * mm});
            skLineSegment(sketch, "E78.5.43", {"start": v(12.68, 5.59) * mm, "end": v(17.38, 2.87) * mm});
            skLineSegment(sketch, "E78.5.44", {"start": v(15.06, 15.61) * mm, "end": v(14.18, 15.61) * mm});
            skLineSegment(sketch, "E78.5.45", {"start": v(19.1, 1.87) * mm, "end": v(20.4, 1.12) * mm});
            skLineSegment(sketch, "E78.5.46", {"start": v(13.53, 0.86) * mm, "end": v(9.01, 3.47) * mm});
            skLineSegment(sketch, "E78.5.47", {"start": v(9.68, 11.29) * mm, "end": v(8.6, 12.37) * mm});
            skLineSegment(sketch, "E78.5.48", {"start": v(15.68, 7.32) * mm, "end": v(18.88, 5.47) * mm});
            skLineSegment(sketch, "E78.5.49", {"start": v(17.38, 2.87) * mm, "end": v(16.94, 2.1) * mm});
            skLineSegment(sketch, "E78.5.50", {"start": v(16.06, 14.61) * mm, "end": v(15.06, 15.61) * mm});
            skLineSegment(sketch, "E78.5.51", {"start": v(17.3, 0.74) * mm, "end": v(18.67, 1.1) * mm});
            skLineSegment(sketch, "E78.5.52", {"start": v(20.68, 6.6) * mm, "end": v(21.05, 5.23) * mm});
            skLineSegment(sketch, "E78.5.53", {"start": v(8.6, 12.37) * mm, "end": v(7.51, 11.29) * mm});
            skPoint(sketch, "E78.5.54", {"position": v(10.3, 14.61) * mm});
            skLineSegment(sketch, "E78.5.55", {"start": v(22.09, 8.02) * mm, "end": v(19.5, 9.52) * mm});
            skLineSegment(sketch, "E78.5.56", {"start": v(18, 15.12) * mm, "end": v(18, 12.12) * mm});
            skLineSegment(sketch, "E78.5.57", {"start": v(15.06, 13.61) * mm, "end": v(16.06, 14.61) * mm});
            skLineSegment(sketch, "E78.5.58", {"start": v(15.01, 1.26) * mm, "end": v(13.53, 0.86) * mm});
            skLineSegment(sketch, "E78.5.59", {"start": v(21.9, 3.72) * mm, "end": v(22.46, 1.67) * mm});
            skLineSegment(sketch, "E78.5.60", {"start": v(7.51, 11.29) * mm, "end": v(7.51, 6.07) * mm});
            skPoint(sketch, "E78.5.61", {"position": v(14.18, 8.18) * mm});
            skLineSegment(sketch, "E78.5.62", {"start": v(18.67, 1.1) * mm, "end": v(16.94, 2.1) * mm, "construction": true});
            skLineSegment(sketch, "E78.5.63", {"start": v(10.3, 15.61) * mm, "end": v(10.3, 13.61) * mm, "construction": true});
            skLineSegment(sketch, "E78.5.64", {"start": v(13.53, 0.86) * mm, "end": v(14.62, 2.74) * mm, "construction": true});
            skLineSegment(sketch, "E78.5.65", {"start": v(15.01, 1.26) * mm, "end": v(14.07, 1.8) * mm, "construction": true});
            skLineSegment(sketch, "E78.5.66", {"start": v(8.6, 12.37) * mm, "end": v(8.6, 11.29) * mm, "construction": true});
            skLineSegment(sketch, "E78.5.67", {"start": v(7.51, 11.29) * mm, "end": v(9.68, 11.29) * mm, "construction": true});
            skLineSegment(sketch, "E78.5.68", {"start": v(17, 15.12) * mm, "end": v(18, 15.12) * mm, "construction": true});
            skLineSegment(sketch, "E78.5.69", {"start": v(17.5, 15.62) * mm, "end": v(17.5, 15.12) * mm, "construction": true});
            skLineSegment(sketch, "E78.5.70", {"start": v(21.59, 7.16) * mm, "end": v(22.09, 8.02) * mm, "construction": true});
            skLineSegment(sketch, "E78.5.71", {"start": v(22.27, 7.34) * mm, "end": v(22.09, 8.02) * mm});
            skLineSegment(sketch, "E78.5.72", {"start": v(17, 15.12) * mm, "end": v(17.5, 15.62) * mm});
            skLineSegment(sketch, "E78.5.73", {"start": v(21.59, 7.16) * mm, "end": v(22.27, 7.34) * mm});
            skLineSegment(sketch, "E78.5.74", {"start": v(17.5, 15.62) * mm, "end": v(18, 15.12) * mm});
            skLineSegment(sketch, "E78.5.75", {"start": v(22.27, 7.34) * mm, "end": v(21.84, 7.59) * mm, "construction": true});
            skPoint(sketch, "E78.center", {"position": v(0, 0) * mm});
            skSolve(sketch);
        }
        {
            var Q0;
            Q0 = qSketchRegion(id + "F0", true);
            extrude(context, id + "F1", {"entities" : qUnion([Q0]), "depth" : 1.5 * mm});
        }
        {
            var Q0;
            Q0=makeQuery(id+"F1.opExtrude","SWEPT_BODY",BODY,{"disambiguationData":[OSD([sQuery(id+"F0.wireOp",EDGE,"E3"),sQuery(id+"F0.wireOp",EDGE,"E4"),sQuery(id+"F0.wireOp",EDGE,"E5"),sQuery(id+"F0.wireOp",EDGE,"E6"),sQuery(id+"F0.wireOp",EDGE,"E7"),sQuery(id+"F0.wireOp",EDGE,"E8"),sQuery(id+"F0.wireOp",EDGE,"E9"),sQuery(id+"F0.wireOp",EDGE,"E10"),sQuery(id+"F0.wireOp",EDGE,"E15.MirrorCS"),sQuery(id+"F0.wireOp",EDGE,"E16.MirrorCS"),sQuery(id+"F0.wireOp",EDGE,"E17.MirrorCS"),sQuery(id+"F0.wireOp",EDGE,"E18.MirrorCS"),sQuery(id+"F0.wireOp",EDGE,"E19.MirrorCS"),sQuery(id+"F0.wireOp",EDGE,"E20.MirrorCS"),sQuery(id+"F0.wireOp",EDGE,"E21.MirrorCS"),sQuery(id+"F0.wireOp",EDGE,"E22"),sQuery(id+"F0.wireOp",EDGE,"E23"),sQuery(id+"F0.wireOp",EDGE,"E24"),sQuery(id+"F0.wireOp",EDGE,"E25"),sQuery(id+"F0.wireOp",EDGE,"E26"),sQuery(id+"F0.wireOp",EDGE,"E27"),sQuery(id+"F0.wireOp",EDGE,"E28"),sQuery(id+"F0.wireOp",EDGE,"E33"),sQuery(id+"F0.wireOp",EDGE,"E34"),sQuery(id+"F0.wireOp",EDGE,"E35"),sQuery(id+"F0.wireOp",EDGE,"E36"),sQuery(id+"F0.wireOp",EDGE,"E40.trimOffspring"),sQuery(id+"F0.wireOp",EDGE,"E42.MirrorCS"),sQuery(id+"F0.wireOp",EDGE,"E43.MirrorCS"),sQuery(id+"F0.wireOp",EDGE,"E48.MirrorCS"),sQuery(id+"F0.wireOp",EDGE,"E49.MirrorCS"),sQuery(id+"F0.wireOp",EDGE,"E50.MirrorCS"),sQuery(id+"F0.wireOp",EDGE,"E51.MirrorCS"),sQuery(id+"F0.wireOp",EDGE,"E52.MirrorCS"),sQuery(id+"F0.wireOp",EDGE,"E53.MirrorCS"),sQuery(id+"F0.wireOp",EDGE,"E55.MirrorCS"),sQuery(id+"F0.wireOp",EDGE,"E56.MirrorCS"),sQuery(id+"F0.wireOp",EDGE,"E57.MirrorCS"),sQuery(id+"F0.wireOp",EDGE,"E58.MirrorCS"),sQuery(id+"F0.wireOp",EDGE,"E60.MirrorCS"),sQuery(id+"F0.wireOp",EDGE,"E61.MirrorCS"),sQuery(id+"F0.wireOp",EDGE,"E64.MirrorCS"),sQuery(id+"F0.wireOp",EDGE,"E65.MirrorCS"),sQuery(id+"F0.wireOp",EDGE,"E66.MirrorCS"),sQuery(id+"F0.wireOp",EDGE,"E68.MirrorCS"),sQuery(id+"F0.wireOp",EDGE,"E69.MirrorCS"),sQuery(id+"F0.wireOp",EDGE,"E70.MirrorCS"),sQuery(id+"F0.wireOp",EDGE,"E71.MirrorCS"),sQuery(id+"F0.wireOp",EDGE,"E72.MirrorCS"),sQuery(id+"F0.wireOp",EDGE,"E73.MirrorCS"),sQuery(id+"F0.wireOp",EDGE,"E74.MirrorCS"),sQuery(id+"F0.wireOp",EDGE,"E75.MirrorCS"),sQuery(id+"F0.wireOp",EDGE,"E76.MirrorCS"),sQuery(id+"F0.wireOp",EDGE,"E77.MirrorCS"),sQuery(id+"F0.wireOp",EDGE,"E78.1.0"),sQuery(id+"F0.wireOp",EDGE,"E78.1.1"),sQuery(id+"F0.wireOp",EDGE,"E78.1.2"),sQuery(id+"F0.wireOp",EDGE,"E78.1.3"),sQuery(id+"F0.wireOp",EDGE,"E78.1.5"),sQuery(id+"F0.wireOp",EDGE,"E78.1.7"),sQuery(id+"F0.wireOp",EDGE,"E78.1.9"),sQuery(id+"F0.wireOp",EDGE,"E78.1.10"),sQuery(id+"F0.wireOp",EDGE,"E78.1.13"),sQuery(id+"F0.wireOp",EDGE,"E78.1.14"),sQuery(id+"F0.wireOp",EDGE,"E78.1.15"),sQuery(id+"F0.wireOp",EDGE,"E78.1.16"),sQuery(id+"F0.wireOp",EDGE,"E78.1.17"),sQuery(id+"F0.wireOp",EDGE,"E78.1.18"),sQuery(id+"F0.wireOp",EDGE,"E78.1.20"),sQuery(id+"F0.wireOp",EDGE,"E78.1.21"),sQuery(id+"F0.wireOp",EDGE,"E78.1.22"),sQuery(id+"F0.wireOp",EDGE,"E78.1.23"),sQuery(id+"F0.wireOp",EDGE,"E78.1.24"),sQuery(id+"F0.wireOp",EDGE,"E78.1.25"),sQuery(id+"F0.wireOp",EDGE,"E78.1.26"),sQuery(id+"F0.wireOp",EDGE,"E78.1.27"),sQuery(id+"F0.wireOp",EDGE,"E78.1.28"),sQuery(id+"F0.wireOp",EDGE,"E78.1.29"),sQuery(id+"F0.wireOp",EDGE,"E78.1.30"),sQuery(id+"F0.wireOp",EDGE,"E78.1.31"),sQuery(id+"F0.wireOp",EDGE,"E78.1.32"),sQuery(id+"F0.wireOp",EDGE,"E78.1.33"),sQuery(id+"F0.wireOp",EDGE,"E78.1.34"),sQuery(id+"F0.wireOp",EDGE,"E78.1.35"),sQuery(id+"F0.wireOp",EDGE,"E78.1.36"),sQuery(id+"F0.wireOp",EDGE,"E78.1.37"),sQuery(id+"F0.wireOp",EDGE,"E78.1.38"),sQuery(id+"F0.wireOp",EDGE,"E78.1.42"),sQuery(id+"F0.wireOp",EDGE,"E78.1.43"),sQuery(id+"F0.wireOp",EDGE,"E78.1.44"),sQuery(id+"F0.wireOp",EDGE,"E78.1.45"),sQuery(id+"F0.wireOp",EDGE,"E78.1.46"),sQuery(id+"F0.wireOp",EDGE,"E78.1.47"),sQuery(id+"F0.wireOp",EDGE,"E78.1.48"),sQuery(id+"F0.wireOp",EDGE,"E78.1.49"),sQuery(id+"F0.wireOp",EDGE,"E78.1.50"),sQuery(id+"F0.wireOp",EDGE,"E78.1.51"),sQuery(id+"F0.wireOp",EDGE,"E78.1.52"),sQuery(id+"F0.wireOp",EDGE,"E78.1.53"),sQuery(id+"F0.wireOp",EDGE,"E78.1.55"),sQuery(id+"F0.wireOp",EDGE,"E78.1.56"),sQuery(id+"F0.wireOp",EDGE,"E78.1.57"),sQuery(id+"F0.wireOp",EDGE,"E78.1.58"),sQuery(id+"F0.wireOp",EDGE,"E78.1.59"),sQuery(id+"F0.wireOp",EDGE,"E78.1.60"),sQuery(id+"F0.wireOp",EDGE,"E78.1.71"),sQuery(id+"F0.wireOp",EDGE,"E78.1.72"),sQuery(id+"F0.wireOp",EDGE,"E78.1.73"),sQuery(id+"F0.wireOp",EDGE,"E78.1.74"),sQuery(id+"F0.wireOp",EDGE,"E78.2.0"),sQuery(id+"F0.wireOp",EDGE,"E78.2.1"),sQuery(id+"F0.wireOp",EDGE,"E78.2.2"),sQuery(id+"F0.wireOp",EDGE,"E78.2.3"),sQuery(id+"F0.wireOp",EDGE,"E78.2.5"),sQuery(id+"F0.wireOp",EDGE,"E78.2.7"),sQuery(id+"F0.wireOp",EDGE,"E78.2.9"),sQuery(id+"F0.wireOp",EDGE,"E78.2.10"),sQuery(id+"F0.wireOp",EDGE,"E78.2.13"),sQuery(id+"F0.wireOp",EDGE,"E78.2.14"),sQuery(id+"F0.wireOp",EDGE,"E78.2.15"),sQuery(id+"F0.wireOp",EDGE,"E78.2.16"),sQuery(id+"F0.wireOp",EDGE,"E78.2.17"),sQuery(id+"F0.wireOp",EDGE,"E78.2.18"),sQuery(id+"F0.wireOp",EDGE,"E78.2.20"),sQuery(id+"F0.wireOp",EDGE,"E78.2.21"),sQuery(id+"F0.wireOp",EDGE,"E78.2.22"),sQuery(id+"F0.wireOp",EDGE,"E78.2.23"),sQuery(id+"F0.wireOp",EDGE,"E78.2.24"),sQuery(id+"F0.wireOp",EDGE,"E78.2.25"),sQuery(id+"F0.wireOp",EDGE,"E78.2.26"),sQuery(id+"F0.wireOp",EDGE,"E78.2.27"),sQuery(id+"F0.wireOp",EDGE,"E78.2.28"),sQuery(id+"F0.wireOp",EDGE,"E78.2.29"),sQuery(id+"F0.wireOp",EDGE,"E78.2.30"),sQuery(id+"F0.wireOp",EDGE,"E78.2.31"),sQuery(id+"F0.wireOp",EDGE,"E78.2.32"),sQuery(id+"F0.wireOp",EDGE,"E78.2.33"),sQuery(id+"F0.wireOp",EDGE,"E78.2.34"),sQuery(id+"F0.wireOp",EDGE,"E78.2.35"),sQuery(id+"F0.wireOp",EDGE,"E78.2.36"),sQuery(id+"F0.wireOp",EDGE,"E78.2.37"),sQuery(id+"F0.wireOp",EDGE,"E78.2.38"),sQuery(id+"F0.wireOp",EDGE,"E78.2.42"),sQuery(id+"F0.wireOp",EDGE,"E78.2.43"),sQuery(id+"F0.wireOp",EDGE,"E78.2.44"),sQuery(id+"F0.wireOp",EDGE,"E78.2.45"),sQuery(id+"F0.wireOp",EDGE,"E78.2.46"),sQuery(id+"F0.wireOp",EDGE,"E78.2.47"),sQuery(id+"F0.wireOp",EDGE,"E78.2.48"),sQuery(id+"F0.wireOp",EDGE,"E78.2.49"),sQuery(id+"F0.wireOp",EDGE,"E78.2.50"),sQuery(id+"F0.wireOp",EDGE,"E78.2.51"),sQuery(id+"F0.wireOp",EDGE,"E78.2.52"),sQuery(id+"F0.wireOp",EDGE,"E78.2.53"),sQuery(id+"F0.wireOp",EDGE,"E78.2.55"),sQuery(id+"F0.wireOp",EDGE,"E78.2.56"),sQuery(id+"F0.wireOp",EDGE,"E78.2.57"),sQuery(id+"F0.wireOp",EDGE,"E78.2.58"),sQuery(id+"F0.wireOp",EDGE,"E78.2.59"),sQuery(id+"F0.wireOp",EDGE,"E78.2.60"),sQuery(id+"F0.wireOp",EDGE,"E78.2.71"),sQuery(id+"F0.wireOp",EDGE,"E78.2.72"),sQuery(id+"F0.wireOp",EDGE,"E78.2.73"),sQuery(id+"F0.wireOp",EDGE,"E78.2.74"),sQuery(id+"F0.wireOp",EDGE,"E78.3.0"),sQuery(id+"F0.wireOp",EDGE,"E78.3.1"),sQuery(id+"F0.wireOp",EDGE,"E78.3.2"),sQuery(id+"F0.wireOp",EDGE,"E78.3.3"),sQuery(id+"F0.wireOp",EDGE,"E78.3.5"),sQuery(id+"F0.wireOp",EDGE,"E78.3.7"),sQuery(id+"F0.wireOp",EDGE,"E78.3.9"),sQuery(id+"F0.wireOp",EDGE,"E78.3.10"),sQuery(id+"F0.wireOp",EDGE,"E78.3.13"),sQuery(id+"F0.wireOp",EDGE,"E78.3.14"),sQuery(id+"F0.wireOp",EDGE,"E78.3.15"),sQuery(id+"F0.wireOp",EDGE,"E78.3.16"),sQuery(id+"F0.wireOp",EDGE,"E78.3.17"),sQuery(id+"F0.wireOp",EDGE,"E78.3.18"),sQuery(id+"F0.wireOp",EDGE,"E78.3.20"),sQuery(id+"F0.wireOp",EDGE,"E78.3.21"),sQuery(id+"F0.wireOp",EDGE,"E78.3.22"),sQuery(id+"F0.wireOp",EDGE,"E78.3.23"),sQuery(id+"F0.wireOp",EDGE,"E78.3.24"),sQuery(id+"F0.wireOp",EDGE,"E78.3.25"),sQuery(id+"F0.wireOp",EDGE,"E78.3.26"),sQuery(id+"F0.wireOp",EDGE,"E78.3.27"),sQuery(id+"F0.wireOp",EDGE,"E78.3.28"),sQuery(id+"F0.wireOp",EDGE,"E78.3.29"),sQuery(id+"F0.wireOp",EDGE,"E78.3.30"),sQuery(id+"F0.wireOp",EDGE,"E78.3.31"),sQuery(id+"F0.wireOp",EDGE,"E78.3.32"),sQuery(id+"F0.wireOp",EDGE,"E78.3.33"),sQuery(id+"F0.wireOp",EDGE,"E78.3.34"),sQuery(id+"F0.wireOp",EDGE,"E78.3.35"),sQuery(id+"F0.wireOp",EDGE,"E78.3.36"),sQuery(id+"F0.wireOp",EDGE,"E78.3.37"),sQuery(id+"F0.wireOp",EDGE,"E78.3.38"),sQuery(id+"F0.wireOp",EDGE,"E78.3.42"),sQuery(id+"F0.wireOp",EDGE,"E78.3.43"),sQuery(id+"F0.wireOp",EDGE,"E78.3.44"),sQuery(id+"F0.wireOp",EDGE,"E78.3.45"),sQuery(id+"F0.wireOp",EDGE,"E78.3.46"),sQuery(id+"F0.wireOp",EDGE,"E78.3.47"),sQuery(id+"F0.wireOp",EDGE,"E78.3.48"),sQuery(id+"F0.wireOp",EDGE,"E78.3.49"),sQuery(id+"F0.wireOp",EDGE,"E78.3.50"),sQuery(id+"F0.wireOp",EDGE,"E78.3.51"),sQuery(id+"F0.wireOp",EDGE,"E78.3.52"),sQuery(id+"F0.wireOp",EDGE,"E78.3.53"),sQuery(id+"F0.wireOp",EDGE,"E78.3.55"),sQuery(id+"F0.wireOp",EDGE,"E78.3.56"),sQuery(id+"F0.wireOp",EDGE,"E78.3.57"),sQuery(id+"F0.wireOp",EDGE,"E78.3.58"),sQuery(id+"F0.wireOp",EDGE,"E78.3.59"),sQuery(id+"F0.wireOp",EDGE,"E78.3.60"),sQuery(id+"F0.wireOp",EDGE,"E78.3.71"),sQuery(id+"F0.wireOp",EDGE,"E78.3.72"),sQuery(id+"F0.wireOp",EDGE,"E78.3.73"),sQuery(id+"F0.wireOp",EDGE,"E78.3.74"),sQuery(id+"F0.wireOp",EDGE,"E78.4.0"),sQuery(id+"F0.wireOp",EDGE,"E78.4.1"),sQuery(id+"F0.wireOp",EDGE,"E78.4.2"),sQuery(id+"F0.wireOp",EDGE,"E78.4.3"),sQuery(id+"F0.wireOp",EDGE,"E78.4.5"),sQuery(id+"F0.wireOp",EDGE,"E78.4.7"),sQuery(id+"F0.wireOp",EDGE,"E78.4.9"),sQuery(id+"F0.wireOp",EDGE,"E78.4.10"),sQuery(id+"F0.wireOp",EDGE,"E78.4.13"),sQuery(id+"F0.wireOp",EDGE,"E78.4.14"),sQuery(id+"F0.wireOp",EDGE,"E78.4.15"),sQuery(id+"F0.wireOp",EDGE,"E78.4.16"),sQuery(id+"F0.wireOp",EDGE,"E78.4.17"),sQuery(id+"F0.wireOp",EDGE,"E78.4.18"),sQuery(id+"F0.wireOp",EDGE,"E78.4.20"),sQuery(id+"F0.wireOp",EDGE,"E78.4.21"),sQuery(id+"F0.wireOp",EDGE,"E78.4.22"),sQuery(id+"F0.wireOp",EDGE,"E78.4.23"),sQuery(id+"F0.wireOp",EDGE,"E78.4.24"),sQuery(id+"F0.wireOp",EDGE,"E78.4.25"),sQuery(id+"F0.wireOp",EDGE,"E78.4.26"),sQuery(id+"F0.wireOp",EDGE,"E78.4.27"),sQuery(id+"F0.wireOp",EDGE,"E78.4.28"),sQuery(id+"F0.wireOp",EDGE,"E78.4.29"),sQuery(id+"F0.wireOp",EDGE,"E78.4.30"),sQuery(id+"F0.wireOp",EDGE,"E78.4.31"),sQuery(id+"F0.wireOp",EDGE,"E78.4.32"),sQuery(id+"F0.wireOp",EDGE,"E78.4.33"),sQuery(id+"F0.wireOp",EDGE,"E78.4.34"),sQuery(id+"F0.wireOp",EDGE,"E78.4.35"),sQuery(id+"F0.wireOp",EDGE,"E78.4.36"),sQuery(id+"F0.wireOp",EDGE,"E78.4.37"),sQuery(id+"F0.wireOp",EDGE,"E78.4.38"),sQuery(id+"F0.wireOp",EDGE,"E78.4.42"),sQuery(id+"F0.wireOp",EDGE,"E78.4.43"),sQuery(id+"F0.wireOp",EDGE,"E78.4.44"),sQuery(id+"F0.wireOp",EDGE,"E78.4.45"),sQuery(id+"F0.wireOp",EDGE,"E78.4.46"),sQuery(id+"F0.wireOp",EDGE,"E78.4.47"),sQuery(id+"F0.wireOp",EDGE,"E78.4.48"),sQuery(id+"F0.wireOp",EDGE,"E78.4.49"),sQuery(id+"F0.wireOp",EDGE,"E78.4.50"),sQuery(id+"F0.wireOp",EDGE,"E78.4.51"),sQuery(id+"F0.wireOp",EDGE,"E78.4.52"),sQuery(id+"F0.wireOp",EDGE,"E78.4.53"),sQuery(id+"F0.wireOp",EDGE,"E78.4.55"),sQuery(id+"F0.wireOp",EDGE,"E78.4.56"),sQuery(id+"F0.wireOp",EDGE,"E78.4.57"),sQuery(id+"F0.wireOp",EDGE,"E78.4.58"),sQuery(id+"F0.wireOp",EDGE,"E78.4.59"),sQuery(id+"F0.wireOp",EDGE,"E78.4.60"),sQuery(id+"F0.wireOp",EDGE,"E78.4.71"),sQuery(id+"F0.wireOp",EDGE,"E78.4.72"),sQuery(id+"F0.wireOp",EDGE,"E78.4.73"),sQuery(id+"F0.wireOp",EDGE,"E78.4.74"),sQuery(id+"F0.wireOp",EDGE,"E78.5.0"),sQuery(id+"F0.wireOp",EDGE,"E78.5.1"),sQuery(id+"F0.wireOp",EDGE,"E78.5.2"),sQuery(id+"F0.wireOp",EDGE,"E78.5.3"),sQuery(id+"F0.wireOp",EDGE,"E78.5.5"),sQuery(id+"F0.wireOp",EDGE,"E78.5.7"),sQuery(id+"F0.wireOp",EDGE,"E78.5.9"),sQuery(id+"F0.wireOp",EDGE,"E78.5.10"),sQuery(id+"F0.wireOp",EDGE,"E78.5.11"),sQuery(id+"F0.wireOp",EDGE,"E78.5.13"),sQuery(id+"F0.wireOp",EDGE,"E78.5.14"),sQuery(id+"F0.wireOp",EDGE,"E78.5.15"),sQuery(id+"F0.wireOp",EDGE,"E78.5.16"),sQuery(id+"F0.wireOp",EDGE,"E78.5.17"),sQuery(id+"F0.wireOp",EDGE,"E78.5.18"),sQuery(id+"F0.wireOp",EDGE,"E78.5.20"),sQuery(id+"F0.wireOp",EDGE,"E78.5.21"),sQuery(id+"F0.wireOp",EDGE,"E78.5.22"),sQuery(id+"F0.wireOp",EDGE,"E78.5.23"),sQuery(id+"F0.wireOp",EDGE,"E78.5.24"),sQuery(id+"F0.wireOp",EDGE,"E78.5.25"),sQuery(id+"F0.wireOp",EDGE,"E78.5.26"),sQuery(id+"F0.wireOp",EDGE,"E78.5.27"),sQuery(id+"F0.wireOp",EDGE,"E78.5.28"),sQuery(id+"F0.wireOp",EDGE,"E78.5.29"),sQuery(id+"F0.wireOp",EDGE,"E78.5.30"),sQuery(id+"F0.wireOp",EDGE,"E78.5.31"),sQuery(id+"F0.wireOp",EDGE,"E78.5.32"),sQuery(id+"F0.wireOp",EDGE,"E78.5.33"),sQuery(id+"F0.wireOp",EDGE,"E78.5.34"),sQuery(id+"F0.wireOp",EDGE,"E78.5.35"),sQuery(id+"F0.wireOp",EDGE,"E78.5.36"),sQuery(id+"F0.wireOp",EDGE,"E78.5.37"),sQuery(id+"F0.wireOp",EDGE,"E78.5.38"),sQuery(id+"F0.wireOp",EDGE,"E78.5.42"),sQuery(id+"F0.wireOp",EDGE,"E78.5.43"),sQuery(id+"F0.wireOp",EDGE,"E78.5.44"),sQuery(id+"F0.wireOp",EDGE,"E78.5.45"),sQuery(id+"F0.wireOp",EDGE,"E78.5.46"),sQuery(id+"F0.wireOp",EDGE,"E78.5.47"),sQuery(id+"F0.wireOp",EDGE,"E78.5.48"),sQuery(id+"F0.wireOp",EDGE,"E78.5.49"),sQuery(id+"F0.wireOp",EDGE,"E78.5.50"),sQuery(id+"F0.wireOp",EDGE,"E78.5.51"),sQuery(id+"F0.wireOp",EDGE,"E78.5.52"),sQuery(id+"F0.wireOp",EDGE,"E78.5.53"),sQuery(id+"F0.wireOp",EDGE,"E78.5.55"),sQuery(id+"F0.wireOp",EDGE,"E78.5.56"),sQuery(id+"F0.wireOp",EDGE,"E78.5.57"),sQuery(id+"F0.wireOp",EDGE,"E78.5.58"),sQuery(id+"F0.wireOp",EDGE,"E78.5.59"),sQuery(id+"F0.wireOp",EDGE,"E78.5.60"),sQuery(id+"F0.wireOp",EDGE,"E78.5.71"),sQuery(id+"F0.wireOp",EDGE,"E78.5.72"),sQuery(id+"F0.wireOp",EDGE,"E78.5.73"),sQuery(id+"F0.wireOp",EDGE,"E78.5.74")])]});
            var Q1;
            Q1=qCreatedBy(makeId("Origin.pointOp"),VERTEX);
            transform(context, id + "F2", {"entities" : qUnion([Q0]), "transformType" : TransformType.SCALE_UNIFORMLY, "scale" : 2, "scalePoint" : qUnion([Q1]), "makeCopy" : false});
        }
    });
